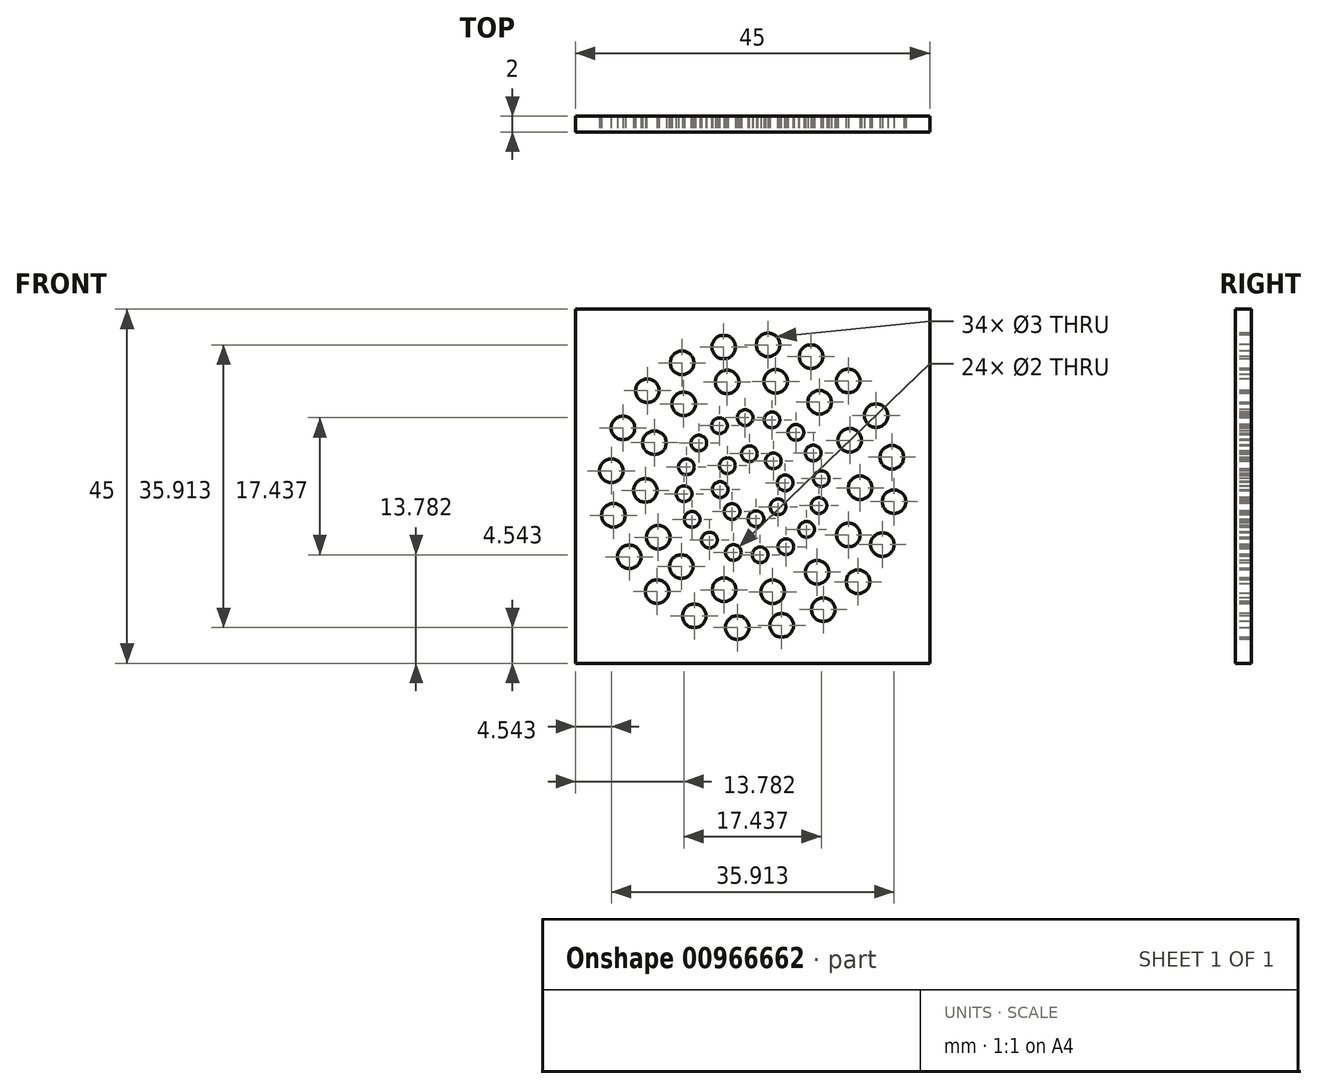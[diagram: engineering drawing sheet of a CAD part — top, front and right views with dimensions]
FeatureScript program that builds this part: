
annotation { "Feature Type Name" : "Feature", "Feature Type Description" : "" }
export const myFeature = defineFeature(function(context is Context, id is Id, definition is map)
    precondition{}
    {
        {
            var Q0;
            Q0=qCreatedBy(makeId("Front.planeOp"),FACE);
            var sketch = newSketch(context, id + "F0", { "sketchPlane" : qUnion([Q0])});
            skLineSegment(sketch, "E0.bottom", {"start": v(0, 0) * mm, "end": v(-45, 0) * mm});
            skLineSegment(sketch, "E0.top", {"start": v(0, 45) * mm, "end": v(-45, 45) * mm});
            skLineSegment(sketch, "E0.left", {"start": v(0, 0) * mm, "end": v(0, 45) * mm});
            skLineSegment(sketch, "E0.right", {"start": v(-45, 0) * mm, "end": v(-45, 45) * mm});
            skSolve(sketch);
        }
        {
            var Q0;
            Q0 = qSketchRegion(id + "F0", true);
            extrude(context, id + "F1", {"entities" : qUnion([Q0]), "depth" : 2 * mm, "offsetDistance" : 25 * mm});
        }
        {
            var Q0;
            Q0=makeQuery(id+"F1.opExtrude","CAP_FACE",FACE,{"disambiguationData":[OSD([sQuery(id+"F0.wireOp",EDGE,"E0.bottom"),sQuery(id+"F0.wireOp",EDGE,"E0.top"),sQuery(id+"F0.wireOp",EDGE,"E0.left"),sQuery(id+"F0.wireOp",EDGE,"E0.right")])],"isStart":false});
            var sketch = newSketch(context, id + "F2", { "sketchPlane" : qUnion([Q0])});
            skLineSegment(sketch, "E1", {"start": v(-45, 45) * mm, "end": v(0, 0) * mm, "construction": true});
            skLineSegment(sketch, "E2", {"start": v(0, 45) * mm, "end": v(-45, 0) * mm, "construction": true});
            skCircle(sketch, "E3", {"center": v(-22.5, 22.5) * mm, "radius": 4.15 * mm, "construction": true});
            skCircle(sketch, "E4", {"center": v(-22.92, 26.63) * mm, "radius": 1 * mm});
            skCircle(sketch, "E5.1.0", {"center": v(-25.71, 25.12) * mm, "radius": 1 * mm});
            skCircle(sketch, "E5.2.0", {"center": v(-26.63, 22.08) * mm, "radius": 1 * mm});
            skCircle(sketch, "E6.1.3.0", {"center": v(-25.12, 19.29) * mm, "radius": 1 * mm});
            skCircle(sketch, "E7", {"center": v(-22.5, 22.5) * mm, "radius": 13.64 * mm, "construction": true});
            skCircle(sketch, "E8", {"center": v(-34.5, 16.01) * mm, "radius": 1.5 * mm});
            skCircle(sketch, "E9.1.0", {"center": v(-36.13, 21.97) * mm, "radius": 1.5 * mm});
            skCircle(sketch, "E9.2.0", {"center": v(-34.97, 28.03) * mm, "radius": 1.5 * mm});
            skLineSegment(sketch, "E9.anchor1", {"start": v(-22.5, 22.5) * mm, "end": v(-34.5, 16.01) * mm, "construction": true});
            skLineSegment(sketch, "E9.anchor2", {"start": v(-22.5, 22.5) * mm, "end": v(-31.56, 12.3) * mm, "construction": true});
            skCircle(sketch, "E10.1.3.0", {"center": v(-31.26, 32.96) * mm, "radius": 1.5 * mm});
            skCircle(sketch, "E10.1.4.0", {"center": v(-25.75, 35.75) * mm, "radius": 1.5 * mm});
            skCircle(sketch, "E10.1.5.0", {"center": v(-19.58, 35.83) * mm, "radius": 1.5 * mm});
            skCircle(sketch, "E11.1.6.0", {"center": v(-14, 33.17) * mm, "radius": 1.5 * mm});
            skCircle(sketch, "E11.1.7.0", {"center": v(-10.17, 28.33) * mm, "radius": 1.5 * mm});
            skCircle(sketch, "E12.1.8.0", {"center": v(-8.86, 22.3) * mm, "radius": 1.5 * mm});
            skCircle(sketch, "E12.1.9.0", {"center": v(-10.34, 16.3) * mm, "radius": 1.5 * mm});
            skCircle(sketch, "E13", {"center": v(-22.5, 22.5) * mm, "radius": 18.06 * mm, "construction": true});
            skCircle(sketch, "E14", {"center": v(-26.19, 40.18) * mm, "radius": 1.5 * mm});
            skCircle(sketch, "E15.1.0", {"center": v(-31.47, 38.18) * mm, "radius": 1.5 * mm});
            skCircle(sketch, "E15.2.0", {"center": v(-35.88, 34.64) * mm, "radius": 1.5 * mm});
            skCircle(sketch, "E16.1.3.0", {"center": v(-38.97, 29.91) * mm, "radius": 1.5 * mm});
            skCircle(sketch, "E16.1.4.0", {"center": v(-40.46, 24.46) * mm, "radius": 1.5 * mm});
            skCircle(sketch, "E16.1.5.0", {"center": v(-40.18, 18.81) * mm, "radius": 1.5 * mm});
            skCircle(sketch, "E16.1.6.0", {"center": v(-38.18, 13.53) * mm, "radius": 1.5 * mm});
            skCircle(sketch, "E16.1.7.0", {"center": v(-34.64, 9.12) * mm, "radius": 1.5 * mm});
            skCircle(sketch, "E16.1.8.0", {"center": v(-29.91, 6.03) * mm, "radius": 1.5 * mm});
            skCircle(sketch, "E16.1.9.0", {"center": v(-24.46, 4.54) * mm, "radius": 1.5 * mm});
            skCircle(sketch, "E16.1.10.0", {"center": v(-18.81, 4.82) * mm, "radius": 1.5 * mm});
            skCircle(sketch, "E16.1.11.0", {"center": v(-13.53, 6.82) * mm, "radius": 1.5 * mm});
            skCircle(sketch, "E17.1.12.0", {"center": v(-9.12, 10.36) * mm, "radius": 1.5 * mm});
            skCircle(sketch, "E17.1.13.0", {"center": v(-6.03, 15.09) * mm, "radius": 1.5 * mm});
            skCircle(sketch, "E17.1.14.0", {"center": v(-4.54, 20.54) * mm, "radius": 1.5 * mm});
            skCircle(sketch, "E17.1.15.0", {"center": v(-4.82, 26.19) * mm, "radius": 1.5 * mm});
            skCircle(sketch, "E18.1.10.0", {"center": v(-14.32, 11.58) * mm, "radius": 1.5 * mm});
            skCircle(sketch, "E18.1.11.0", {"center": v(-19.97, 9.1) * mm, "radius": 1.5 * mm});
            skCircle(sketch, "E19.1.12.0", {"center": v(-26.14, 9.35) * mm, "radius": 1.5 * mm});
            skCircle(sketch, "E19.1.13.0", {"center": v(-31.56, 12.3) * mm, "radius": 1.5 * mm});
            skCircle(sketch, "E20.1.16.0", {"center": v(-6.82, 31.47) * mm, "radius": 1.5 * mm});
            skCircle(sketch, "E20.1.17.0", {"center": v(-10.36, 35.88) * mm, "radius": 1.5 * mm});
            skCircle(sketch, "E20.1.18.0", {"center": v(-15.09, 38.97) * mm, "radius": 1.5 * mm});
            skCircle(sketch, "E20.1.19.0", {"center": v(-20.54, 40.46) * mm, "radius": 1.5 * mm});
            skCircle(sketch, "E21", {"center": v(-22.5, 22.5) * mm, "radius": 8.77 * mm, "construction": true});
            skCircle(sketch, "E22", {"center": v(-26.72, 30.19) * mm, "radius": 1 * mm});
            skCircle(sketch, "E23.1.0", {"center": v(-29.34, 27.99) * mm, "radius": 1 * mm});
            skCircle(sketch, "E23.2.0", {"center": v(-30.92, 24.95) * mm, "radius": 1 * mm});
            skCircle(sketch, "E24.1.3.0", {"center": v(-31.22, 21.55) * mm, "radius": 1 * mm});
            skCircle(sketch, "E24.1.4.0", {"center": v(-30.19, 18.28) * mm, "radius": 1 * mm});
            skCircle(sketch, "E24.1.5.0", {"center": v(-27.99, 15.66) * mm, "radius": 1 * mm});
            skCircle(sketch, "E25.1.6.0", {"center": v(-24.95, 14.08) * mm, "radius": 1 * mm});
            skCircle(sketch, "E25.1.7.0", {"center": v(-21.55, 13.78) * mm, "radius": 1 * mm});
            skCircle(sketch, "E25.1.8.0", {"center": v(-18.28, 14.81) * mm, "radius": 1 * mm});
            skCircle(sketch, "E25.1.9.0", {"center": v(-15.66, 17.01) * mm, "radius": 1 * mm});
            skCircle(sketch, "E26.1.4.0", {"center": v(-22.08, 18.37) * mm, "radius": 1 * mm});
            skCircle(sketch, "E26.1.5.0", {"center": v(-19.29, 19.88) * mm, "radius": 1 * mm});
            skCircle(sketch, "E26.1.6.0", {"center": v(-18.37, 22.92) * mm, "radius": 1 * mm});
            skCircle(sketch, "E26.1.7.0", {"center": v(-19.88, 25.71) * mm, "radius": 1 * mm});
            skCircle(sketch, "E27.1.10.0", {"center": v(-14.08, 20.05) * mm, "radius": 1 * mm});
            skCircle(sketch, "E27.1.11.0", {"center": v(-13.78, 23.45) * mm, "radius": 1 * mm});
            skCircle(sketch, "E27.1.12.0", {"center": v(-14.81, 26.72) * mm, "radius": 1 * mm});
            skCircle(sketch, "E27.1.13.0", {"center": v(-17.01, 29.34) * mm, "radius": 1 * mm});
            skCircle(sketch, "E27.1.14.0", {"center": v(-20.05, 30.92) * mm, "radius": 1 * mm});
            skCircle(sketch, "E27.1.15.0", {"center": v(-23.45, 31.22) * mm, "radius": 1 * mm});
            skSolve(sketch);
        }
        {
            var Q0;
            Q0=makeQuery(id+"F2.imprint","IMPRINT",FACE,{"disambiguationData":[TD([[makeQuery(id+"F2.imprint","IMPRINT",EDGE,{"derivedFrom":sQuery(id+"F2.wireOp",EDGE,"E5.2.0")}),1.0]])]});
            var Q1;
            Q1=makeQuery(id+"F2.imprint","IMPRINT",FACE,{"disambiguationData":[TD([[makeQuery(id+"F2.imprint","IMPRINT",EDGE,{"derivedFrom":sQuery(id+"F2.wireOp",EDGE,"E5.1.0")}),1.0]])]});
            var Q2;
            Q2=makeQuery(id+"F2.imprint","IMPRINT",FACE,{"disambiguationData":[TD([[makeQuery(id+"F2.imprint","IMPRINT",EDGE,{"derivedFrom":sQuery(id+"F2.wireOp",EDGE,"E4")}),1.0]])]});
            var Q3;
            Q3=makeQuery(id+"F2.imprint","IMPRINT",FACE,{"disambiguationData":[TD([[makeQuery(id+"F2.imprint","IMPRINT",EDGE,{"derivedFrom":sQuery(id+"F2.wireOp",EDGE,"E6.1.3.0")}),1.0]])]});
            var Q4;
            Q4=makeQuery(id+"F2.imprint","IMPRINT",FACE,{"disambiguationData":[TD([[makeQuery(id+"F2.imprint","IMPRINT",EDGE,{"derivedFrom":sQuery(id+"F2.wireOp",EDGE,"E12.1.9.0")}),1.0]])]});
            var Q5;
            Q5=makeQuery(id+"F2.imprint","IMPRINT",FACE,{"disambiguationData":[TD([[makeQuery(id+"F2.imprint","IMPRINT",EDGE,{"derivedFrom":sQuery(id+"F2.wireOp",EDGE,"E12.1.8.0")}),1.0]])]});
            var Q6;
            Q6=makeQuery(id+"F2.imprint","IMPRINT",FACE,{"disambiguationData":[TD([[makeQuery(id+"F2.imprint","IMPRINT",EDGE,{"derivedFrom":sQuery(id+"F2.wireOp",EDGE,"E11.1.7.0")}),1.0]])]});
            var Q7;
            Q7=makeQuery(id+"F2.imprint","IMPRINT",FACE,{"disambiguationData":[TD([[makeQuery(id+"F2.imprint","IMPRINT",EDGE,{"derivedFrom":sQuery(id+"F2.wireOp",EDGE,"E11.1.6.0")}),1.0]])]});
            var Q8;
            Q8=makeQuery(id+"F2.imprint","IMPRINT",FACE,{"disambiguationData":[TD([[makeQuery(id+"F2.imprint","IMPRINT",EDGE,{"derivedFrom":sQuery(id+"F2.wireOp",EDGE,"E8")}),1.0]])]});
            var Q9;
            Q9=makeQuery(id+"F2.imprint","IMPRINT",FACE,{"disambiguationData":[TD([[makeQuery(id+"F2.imprint","IMPRINT",EDGE,{"derivedFrom":sQuery(id+"F2.wireOp",EDGE,"E16.1.4.0")}),1.0]])]});
            var Q10;
            Q10=makeQuery(id+"F2.imprint","IMPRINT",FACE,{"disambiguationData":[TD([[makeQuery(id+"F2.imprint","IMPRINT",EDGE,{"derivedFrom":sQuery(id+"F2.wireOp",EDGE,"E16.1.5.0")}),1.0]])]});
            var Q11;
            Q11=makeQuery(id+"F2.imprint","IMPRINT",FACE,{"disambiguationData":[TD([[makeQuery(id+"F2.imprint","IMPRINT",EDGE,{"derivedFrom":sQuery(id+"F2.wireOp",EDGE,"E16.1.8.0")}),1.0]])]});
            var Q12;
            Q12=makeQuery(id+"F2.imprint","IMPRINT",FACE,{"disambiguationData":[TD([[makeQuery(id+"F2.imprint","IMPRINT",EDGE,{"derivedFrom":sQuery(id+"F2.wireOp",EDGE,"E10.1.5.0")}),1.0]])]});
            var Q13;
            Q13=makeQuery(id+"F2.imprint","IMPRINT",FACE,{"disambiguationData":[TD([[makeQuery(id+"F2.imprint","IMPRINT",EDGE,{"derivedFrom":sQuery(id+"F2.wireOp",EDGE,"E16.1.10.0")}),1.0]])]});
            var Q14;
            Q14=makeQuery(id+"F2.imprint","IMPRINT",FACE,{"disambiguationData":[TD([[makeQuery(id+"F2.imprint","IMPRINT",EDGE,{"derivedFrom":sQuery(id+"F2.wireOp",EDGE,"E16.1.6.0")}),1.0]])]});
            var Q15;
            Q15=makeQuery(id+"F2.imprint","IMPRINT",FACE,{"disambiguationData":[TD([[makeQuery(id+"F2.imprint","IMPRINT",EDGE,{"derivedFrom":sQuery(id+"F2.wireOp",EDGE,"E16.1.7.0")}),1.0]])]});
            var Q16;
            Q16=makeQuery(id+"F2.imprint","IMPRINT",FACE,{"disambiguationData":[TD([[makeQuery(id+"F2.imprint","IMPRINT",EDGE,{"derivedFrom":sQuery(id+"F2.wireOp",EDGE,"E16.1.9.0")}),1.0]])]});
            var Q17;
            Q17=makeQuery(id+"F2.imprint","IMPRINT",FACE,{"disambiguationData":[TD([[makeQuery(id+"F2.imprint","IMPRINT",EDGE,{"derivedFrom":sQuery(id+"F2.wireOp",EDGE,"E10.1.4.0")}),1.0]])]});
            var Q18;
            Q18=makeQuery(id+"F2.imprint","IMPRINT",FACE,{"disambiguationData":[TD([[makeQuery(id+"F2.imprint","IMPRINT",EDGE,{"derivedFrom":sQuery(id+"F2.wireOp",EDGE,"E10.1.3.0")}),1.0]])]});
            var Q19;
            Q19=makeQuery(id+"F2.imprint","IMPRINT",FACE,{"disambiguationData":[TD([[makeQuery(id+"F2.imprint","IMPRINT",EDGE,{"derivedFrom":sQuery(id+"F2.wireOp",EDGE,"E16.1.3.0")}),1.0]])]});
            var Q20;
            Q20=makeQuery(id+"F2.imprint","IMPRINT",FACE,{"disambiguationData":[TD([[makeQuery(id+"F2.imprint","IMPRINT",EDGE,{"derivedFrom":sQuery(id+"F2.wireOp",EDGE,"E9.1.0")}),1.0]])]});
            var Q21;
            Q21=makeQuery(id+"F2.imprint","IMPRINT",FACE,{"disambiguationData":[TD([[makeQuery(id+"F2.imprint","IMPRINT",EDGE,{"derivedFrom":sQuery(id+"F2.wireOp",EDGE,"E9.2.0")}),1.0]])]});
            var Q22;
            Q22=makeQuery(id+"F2.imprint","IMPRINT",FACE,{"disambiguationData":[TD([[makeQuery(id+"F2.imprint","IMPRINT",EDGE,{"derivedFrom":sQuery(id+"F2.wireOp",EDGE,"E16.1.11.0")}),1.0]])]});
            var Q23;
            Q23=makeQuery(id+"F2.imprint","IMPRINT",FACE,{"disambiguationData":[TD([[makeQuery(id+"F2.imprint","IMPRINT",EDGE,{"derivedFrom":sQuery(id+"F2.wireOp",EDGE,"E14")}),1.0]])]});
            var Q24;
            Q24=makeQuery(id+"F2.imprint","IMPRINT",FACE,{"disambiguationData":[TD([[makeQuery(id+"F2.imprint","IMPRINT",EDGE,{"derivedFrom":sQuery(id+"F2.wireOp",EDGE,"E15.1.0")}),1.0]])]});
            var Q25;
            Q25=makeQuery(id+"F2.imprint","IMPRINT",FACE,{"disambiguationData":[TD([[makeQuery(id+"F2.imprint","IMPRINT",EDGE,{"derivedFrom":sQuery(id+"F2.wireOp",EDGE,"E15.2.0")}),1.0]])]});
            var Q26;
            Q26=makeQuery(id+"F2.imprint","IMPRINT",FACE,{"disambiguationData":[TD([[makeQuery(id+"F2.imprint","IMPRINT",EDGE,{"derivedFrom":sQuery(id+"F2.wireOp",EDGE,"1e078618-5d3f-4fc2-8c69-f84a5c2c7753.1.11.0")}),1.0]])]});
            var Q27;
            Q27=makeQuery(id+"F2.imprint","IMPRINT",FACE,{"disambiguationData":[TD([[makeQuery(id+"F2.imprint","IMPRINT",EDGE,{"derivedFrom":sQuery(id+"F2.wireOp",EDGE,"1e078618-5d3f-4fc2-8c69-f84a5c2c7753.1.10.0")}),1.0]])]});
            var Q28;
            Q28=makeQuery(id+"F2.imprint","IMPRINT",FACE,{"disambiguationData":[TD([[makeQuery(id+"F2.imprint","IMPRINT",EDGE,{"derivedFrom":sQuery(id+"F2.wireOp",EDGE,"E17.1.12.0")}),1.0]])]});
            var Q29;
            Q29=makeQuery(id+"F2.imprint","IMPRINT",FACE,{"disambiguationData":[TD([[makeQuery(id+"F2.imprint","IMPRINT",EDGE,{"derivedFrom":sQuery(id+"F2.wireOp",EDGE,"E17.1.13.0")}),1.0]])]});
            var Q30;
            Q30=makeQuery(id+"F2.imprint","IMPRINT",FACE,{"disambiguationData":[TD([[makeQuery(id+"F2.imprint","IMPRINT",EDGE,{"derivedFrom":sQuery(id+"F2.wireOp",EDGE,"E17.1.14.0")}),1.0]])]});
            var Q31;
            Q31=makeQuery(id+"F2.imprint","IMPRINT",FACE,{"disambiguationData":[TD([[makeQuery(id+"F2.imprint","IMPRINT",EDGE,{"derivedFrom":sQuery(id+"F2.wireOp",EDGE,"E17.1.15.0")}),1.0]])]});
            var Q32;
            Q32=sQuery(id+"F2.wireOp",EDGE,"E4");
            var Q33;
            Q33=sQuery(id+"F2.wireOp",EDGE,"E6.1.3.0");
            var Q34;
            Q34=sQuery(id+"F2.wireOp",EDGE,"E5.2.0");
            var Q35;
            Q35=sQuery(id+"F2.wireOp",EDGE,"E5.1.0");
            extrude(context, id + "F3", {"entities" : qUnion([Q0, Q1, Q2, Q3, Q4, Q5, Q6, Q7, Q8, Q9, Q10, Q11, Q12, Q13, Q14, Q15, Q16, Q17, Q18, Q19, Q20, Q21, Q22, Q23, Q24, Q25, Q26, Q27, Q28, Q29, Q30, Q31]), "operationType" : NewBodyOperationType.REMOVE, "surfaceEntities" : qUnion([Q32, Q33, Q34, Q35]), "oppositeDirection" : true, "depth" : 19.6 * mm, "offsetDistance" : 25 * mm});
        }
        {
            var Q0;
            Q0 = qSketchRegion(id + "F2", true);
            extrude(context, id + "F4", {"entities" : qUnion([Q0]), "operationType" : NewBodyOperationType.REMOVE, "oppositeDirection" : true, "depth" : 25 * mm, "offsetDistance" : 25 * mm});
        }
    });
